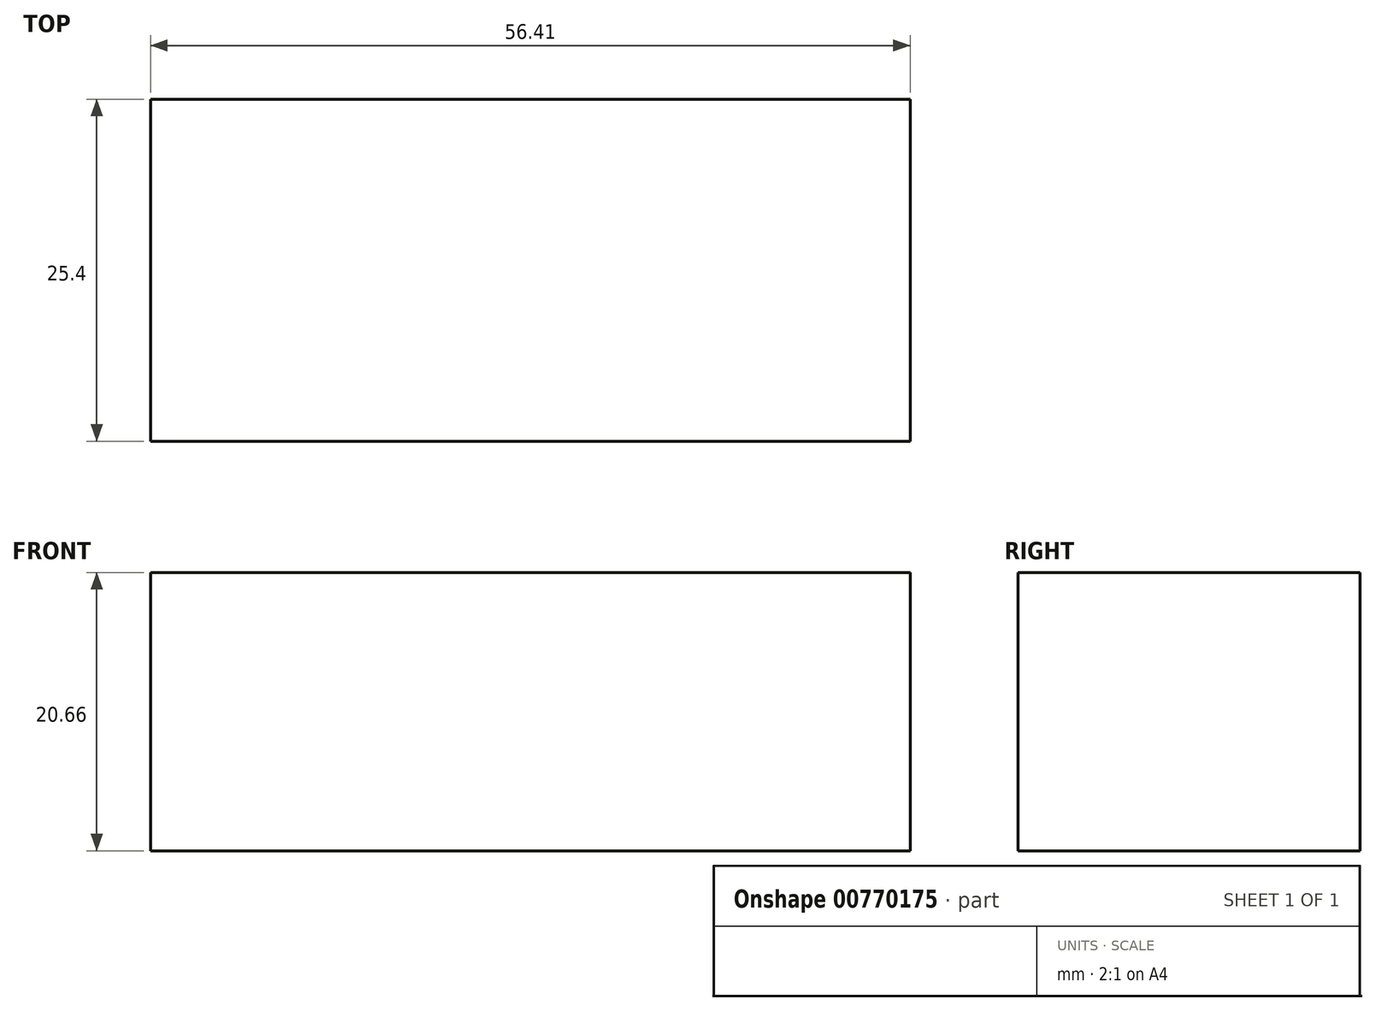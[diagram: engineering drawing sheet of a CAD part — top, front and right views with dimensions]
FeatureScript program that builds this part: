
annotation { "Feature Type Name" : "Feature", "Feature Type Description" : "" }
export const myFeature = defineFeature(function(context is Context, id is Id, definition is map)
    precondition{}
    {
        {
            var Q0;
            Q0=qCreatedBy(makeId("Front.planeOp"),FACE);
            var sketch = newSketch(context, id + "F0", { "sketchPlane" : qUnion([Q0])});
            skLineSegment(sketch, "E0.bottom", {"start": v(55.56, 10.33) * mm, "end": v(16.94, 10.33) * mm});
            skLineSegment(sketch, "E0.top", {"start": v(55.56, -10.33) * mm, "end": v(16.94, -10.33) * mm});
            skLineSegment(sketch, "E0.left", {"start": v(55.56, 10.33) * mm, "end": v(55.56, -10.33) * mm});
            skLineSegment(sketch, "E0.right", {"start": v(16.94, 10.33) * mm, "end": v(16.94, -10.33) * mm});
            skPoint(sketch, "E0.middle", {"position": v(36.25, 0) * mm});
            skLineSegment(sketch, "E1.bottom", {"start": v(22.19, 10.33) * mm, "end": v(-0.85, 10.33) * mm});
            skLineSegment(sketch, "E1.top", {"start": v(22.19, -10.33) * mm, "end": v(-0.85, -10.33) * mm});
            skLineSegment(sketch, "E1.left", {"start": v(22.19, 10.33) * mm, "end": v(22.19, -10.33) * mm});
            skLineSegment(sketch, "E1.right", {"start": v(-0.85, 10.33) * mm, "end": v(-0.85, -10.33) * mm});
            skPoint(sketch, "E1.middle", {"position": v(10.67, 0) * mm});
            skSolve(sketch);
        }
        {
            var Q0;
            Q0 = qSketchRegion(id + "F0", true);
            extrude(context, id + "F1", {"entities" : qUnion([Q0]), "depth" : 25.4 * mm, "offsetDistance" : 25.4 * mm});
        }
    });
